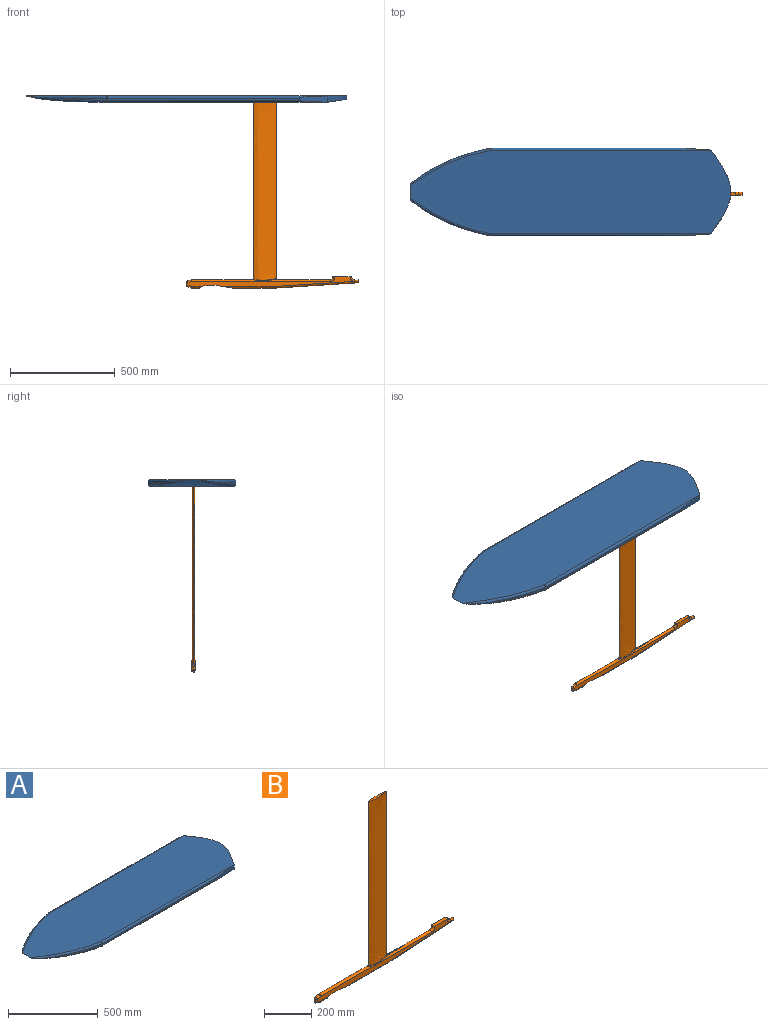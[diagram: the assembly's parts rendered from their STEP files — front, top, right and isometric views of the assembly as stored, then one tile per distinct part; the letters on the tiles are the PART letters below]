
ASSEMBLY  parts=2 mates=1
PART A: 30 faces, bbox 1560.5x427.5x43.4 mm
  f0: plane 400x85.74mm, normal (0.15,0,-0.99), area 23247.7mm2, adj f1,f7,f14,f17
  f1: cylinder r=10mm len=102.9mm, axis (0,-1,0), area 772.3mm2, adj f0,f2,f14,f17
  f2: plane 7.36x5.63mm, normal (1,0,0), area 41.5mm2, adj f1,f8,f14,f17
  f3: plane 918.38x10mm, normal (0,-1,0), area 9183.8mm2, adj f4,f5,f16,f18
  f4: cylinder r=10mm len=1050.06mm, axis (1,0,0), area 15460.1mm2, adj f3,f7,f16,f20
  f5: cylinder r=10mm len=1050.06mm, axis (-1,0,0), area 15460.1mm2, adj f3,f8,f16,f19
  f6: extruded ~379.57x338.9mm, area 84638.6mm2, adj f7,f8,f21,f22,f23,f24,f25,f27
  f7: plane 1098.98x400.02mm, normal (0,0,-1), area 439107.3mm2, adj f0,f4,f6,f11,f22,f24
  f8: plane 1536.86x400.02mm, normal (0,0,1), area 546705.1mm2, adj f2,f5,f6,f10,f14,f17,f21,f27
  f9: plane 918.38x10mm, normal (0,1,0), area 9183.8mm2, adj f10,f11,f15,f28
  f10: cylinder r=10mm len=1050.06mm, axis (1,0,0), area 15460.1mm2, adj f8,f9,f15,f29
  f11: cylinder r=10mm len=1050.06mm, axis (-1,0,0), area 15460.1mm2, adj f7,f9,f15,f26
  f12: extruded ~272.03x95.9mm, area 1948.5mm2, adj f18,f21,f22,f23
  f13: extruded ~272.03x95.9mm, area 1948.5mm2, adj f24,f25,f27,f28
  f14: extruded ~197.18x94.27mm, area 4586.5mm2, adj f0,f1,f2,f8,f16
  f15: extruded ~131.68x30mm, area 2642.1mm2, adj f9,f10,f11,f17
  f16: extruded ~131.68x30mm, area 2642.1mm2, adj f3,f4,f5,f14
  f17: extruded ~197.18x94.27mm, area 4586.5mm2, adj f0,f1,f2,f8,f15
  f18: cylinder r=10mm len=10mm, axis (0,0,1), area 18.3mm2, adj f3,f12,f19,f20
  f19: sphere r=10mm, area 18.3mm2, adj f5,f18,f21
  f20: sphere r=10mm, area 18.3mm2, adj f4,f18,f22
  f21: bspline ~433.46x193.83mm, area 6078.6mm2, adj f6,f8,f12,f19,f23
  f22: bspline ~96.96x29.88mm, area 789.2mm2, adj f6,f7,f12,f20,f23
  f23: bspline ~375.03x177.58mm, area 4755.1mm2, adj f6,f12,f21,f22
  f24: bspline ~96.96x29.88mm, area 789.2mm2, adj f6,f7,f13,f25,f26
  f25: bspline ~375.74x177.97mm, area 4755.1mm2, adj f6,f13,f24,f27
  f26: sphere r=10mm, area 18.3mm2, adj f11,f24,f28
  f27: bspline ~433.46x193.83mm, area 6078.6mm2, adj f6,f8,f13,f25,f29
  f28: cylinder r=10mm len=10mm, axis (0,0,1), area 18.3mm2, adj f9,f13,f26,f29
  f29: sphere r=10mm, area 18.3mm2, adj f10,f27,f28
PART B: 28 faces, bbox 821.4x16.8x888.3 mm
  f0: cylinder r=7.94mm len=256.94mm, axis (1,0,0), area 5656.5mm2, adj f5,f6,f10,f27
  f1: cylinder r=7.94mm len=660.74mm, axis (-1,0,0), area 14592.2mm2, adj f5,f6,f15,f16,f25,f26
  f2: plane 90x15.88mm, normal (0,0,1), area 1374.7mm2, adj f5,f6,f13,f17
  f3: plane 13.42x0.64mm, normal (-1,0,0), area 8.4mm2, adj f18,f19,f20,f21
  f4: plane 16.81x15.96mm, normal (1,0,0), area 184mm2, adj f10,f11
  f5: plane 798.48x47.1mm, normal (0,-1,0), area 16136.1mm2, adj f0,f1,f2,f7,f9,f10,f11,f12
  f6: plane 798.48x47.1mm, normal (0,1,0), area 16136.1mm2, adj f0,f1,f2,f7,f9,f10,f11,f12
  f7: cylinder r=7.94mm len=21.23mm, axis (-0.96,0,0.29), area 493.2mm2, adj f5,f6,f8,f19
  f8: sphere r=7.94mm, area 72.6mm2, adj f7,f9
  f9: cylinder r=7.94mm len=49.03mm, axis (1,0,0), area 1022.9mm2, adj f5,f6,f8,f27
  f10: cylinder r=7.94mm len=390.73mm, axis (1,0,0.06), area 9744.6mm2, adj f0,f4,f5,f6,f11
  f11: cylinder r=7.94mm len=17.3mm, axis (-1,0,0), area 425.2mm2, adj f4,f5,f6,f10,f12
  f12: torus R=20.64mm, axis (0,-1,0), area 610.4mm2, adj f5,f6,f11,f13
  f13: cylinder r=7.94mm len=15.88mm, axis (0,0,1), area 57.4mm2, adj f2,f5,f6,f12
  f14: cylinder r=7.94mm len=21.23mm, axis (0.96,0,0.29), area 493.2mm2, adj f5,f6,f15,f20
  f15: sphere r=7.94mm, area 36.7mm2, adj f1,f14
  f16: torus R=20.64mm, axis (0,-1,0), area 610.4mm2, adj f1,f5,f6,f17
  f17: cylinder r=7.94mm len=15.88mm, axis (0,0,-1), area 57.4mm2, adj f2,f5,f6,f16
  f18: cylinder r=7.62mm len=12.76mm, axis (0,0,1), area 152.7mm2, adj f3,f5,f19,f20
  f19: bspline ~15.88x7.63mm, area 159.4mm2, adj f3,f7,f18,f21
  f20: bspline ~15.88x7.63mm, area 159.4mm2, adj f3,f14,f18,f21
  f21: cylinder r=7.62mm len=12.76mm, axis (0,0,-1), area 152.7mm2, adj f3,f6,f19,f20
  f22: extruded ~843.25x110mm, area 94159.4mm2, adj f23,f24,f26
  f23: extruded ~843.25x110mm, area 94159.4mm2, adj f22,f24,f25
  f24: plane 110x13.94mm, normal (0,0,1), area 1025.8mm2, adj f22,f23
  f25: bspline ~218.81x12.66mm, area 744.5mm2, adj f1,f23,f26
  f26: bspline ~218.53x12.66mm, area 743.9mm2, adj f1,f22,f25
  f27: extruded ~155x15.88mm, area 2355.1mm2, adj f0,f5,f6,f9
PLACE A t=(136.2,-0.48,10.78)mm
PLACE B t=(541.93,-7.29,10.78)mm
MATE fastened B.f24 <-> A.f7  axis (0,0,1) through (595.55,-0.48,10.78)mm
